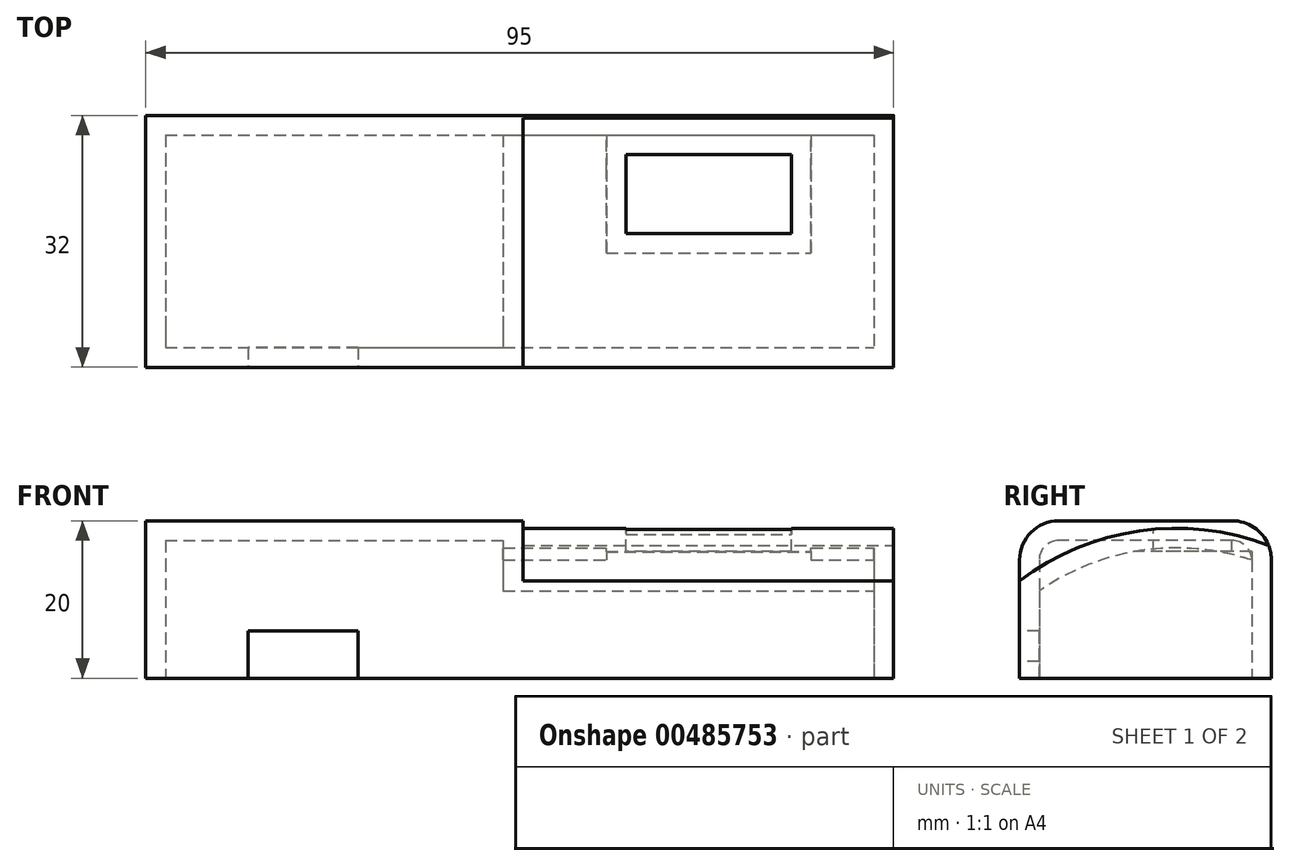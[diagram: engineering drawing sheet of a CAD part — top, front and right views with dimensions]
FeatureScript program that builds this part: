
annotation { "Feature Type Name" : "Feature", "Feature Type Description" : "" }
export const myFeature = defineFeature(function(context is Context, id is Id, definition is map)
    precondition{}
    {
        {
            var Q0;
            Q0=qCreatedBy(makeId("Top.planeOp"),FACE);
            var sketch = newSketch(context, id + "F0", { "sketchPlane" : qUnion([Q0])});
            skLineSegment(sketch, "E0.bottom", {"start": v(19.4, -5.9) * mm, "end": v(114.4, -5.9) * mm});
            skLineSegment(sketch, "E0.top", {"start": v(19.4, -37.9) * mm, "end": v(114.4, -37.9) * mm});
            skLineSegment(sketch, "E0.left", {"start": v(19.4, -5.9) * mm, "end": v(19.4, -37.9) * mm});
            skLineSegment(sketch, "E0.right", {"start": v(114.4, -5.9) * mm, "end": v(114.4, -37.9) * mm});
            skSolve(sketch);
        }
        {
            var Q0;
            Q0=makeQuery(id+"F0.imprint","IMPRINT",FACE,{"disambiguationData":[TD([[makeQuery(id+"F0.imprint","IMPRINT",EDGE,{"derivedFrom":sQuery(id+"F0.wireOp",EDGE,"E0.bottom")}),-1.0]])]});
            extrude(context, id + "F1", {"entities" : qUnion([Q0]), "depth" : 20 * mm});
        }
        {
            var Q0;
            Q0=makeQuery(id+"F1.opExtrude","SWEPT_FACE",FACE,{"disambiguationData":[OSD([sQuery(id+"F0.wireOp",EDGE,"E0.right")])]});
            var sketch = newSketch(context, id + "F2", { "sketchPlane" : qUnion([Q0])});
            skArc(sketch, "E1", {"start": v(-5.9, 16.74) * mm, "mid": v(-22.48, 18.74) * mm, "end": v(-37.9, 12.33) * mm});
            skSolve(sketch);
        }
        {
            var Q0;
            Q0=makeQuery(id+"F1.opExtrude","CAP_EDGE",EDGE,{"disambiguationData":[OSD([sQuery(id+"F0.wireOp",EDGE,"E0.top")])],"isStart":false});
            fillet(context, id + "F3", {"entities" : qUnion([Q0]), "radius" : 5 * mm, "tangentPropagation" : true, "allowEdgeOverflow" : false});
        }
        {
            var Q0;
            Q0=makeQuery(id+"F1.opExtrude","CAP_EDGE",EDGE,{"disambiguationData":[OSD([sQuery(id+"F0.wireOp",EDGE,"E0.bottom")])],"isStart":false});
            fillet(context, id + "F4", {"entities" : qUnion([Q0]), "radius" : 5 * mm, "tangentPropagation" : true, "allowEdgeOverflow" : false});
        }
        {
            var Q0;
            Q0=makeQuery(id+"F1.opExtrude","CAP_FACE",FACE,{"disambiguationData":[OSD([sQuery(id+"F0.wireOp",EDGE,"E0.bottom"),sQuery(id+"F0.wireOp",EDGE,"E0.top"),sQuery(id+"F0.wireOp",EDGE,"E0.left"),sQuery(id+"F0.wireOp",EDGE,"E0.right")])],"isStart":false});
            var sketch = newSketch(context, id + "F5", { "sketchPlane" : qUnion([Q0])});
            skLineSegment(sketch, "E2.bottom", {"start": v(114.4, -10.9) * mm, "end": v(101.4, -10.9) * mm});
            skLineSegment(sketch, "E2.top", {"start": v(114.4, -20.66) * mm, "end": v(101.4, -20.66) * mm});
            skLineSegment(sketch, "E2.left", {"start": v(114.4, -10.9) * mm, "end": v(114.4, -20.66) * mm});
            skLineSegment(sketch, "E2.right", {"start": v(101.4, -10.9) * mm, "end": v(101.4, -20.66) * mm});
            skLineSegment(sketch, "E3.bottom", {"start": v(101.4, -10.9) * mm, "end": v(80.4, -10.9) * mm});
            skLineSegment(sketch, "E3.top", {"start": v(101.4, -20.9) * mm, "end": v(80.4, -20.9) * mm});
            skLineSegment(sketch, "E3.left", {"start": v(101.4, -10.9) * mm, "end": v(101.4, -20.9) * mm});
            skLineSegment(sketch, "E3.right", {"start": v(80.4, -10.9) * mm, "end": v(80.4, -20.9) * mm});
            skSolve(sketch);
        }
        {
            var Q0;
            {var subQ3=sQuery(id+"F5.wireOp",EDGE,"E3.bottom");Q0=makeQuery(id+"F5.imprint","IMPRINT",FACE,{"disambiguationData":[TD([[makeQuery(id+"F5.imprint","IMPRINT",EDGE,{"derivedFrom":subQ3}),1.0]])]});}
            extrude(context, id + "F6", {"entities" : qUnion([Q0]), "operationType" : NewBodyOperationType.REMOVE, "oppositeDirection" : true, "depth" : 25 * mm});
        }
        {
            var Q0;
            {var subQ0=sQuery(id+"F2.wireOp",EDGE,"E1");Q0=makeQuery(id+"F2.imprint","IMPRINT",FACE,{"disambiguationData":[TD([[makeQuery(id+"F2.imprint","IMPRINT",EDGE,{"derivedFrom":subQ0}),-1.0]])]});}
            extrude(context, id + "F7", {"entities" : qUnion([Q0]), "operationType" : NewBodyOperationType.REMOVE, "oppositeDirection" : true, "depth" : 47.1 * mm});
        }
        {
            var Q0;
            Q0=makeQuery(id+"F1.opExtrude","CAP_FACE",FACE,{"disambiguationData":[OSD([sQuery(id+"F0.wireOp",EDGE,"E0.bottom"),sQuery(id+"F0.wireOp",EDGE,"E0.top"),sQuery(id+"F0.wireOp",EDGE,"E0.left"),sQuery(id+"F0.wireOp",EDGE,"E0.right")])],"isStart":true});
            shell(context, id + "F8", {"entities" : qUnion([Q0]), "thickness" : 2.5 * mm});
        }
        {
            var Q0;
            Q0=makeQuery(id+"F1.opExtrude","CAP_FACE",FACE,{"disambiguationData":[OSD([sQuery(id+"F0.wireOp",EDGE,"E0.bottom"),sQuery(id+"F0.wireOp",EDGE,"E0.top"),sQuery(id+"F0.wireOp",EDGE,"E0.left"),sQuery(id+"F0.wireOp",EDGE,"E0.right")])],"isStart":true});
            var sketch = newSketch(context, id + "F9", { "sketchPlane" : qUnion([Q0])});
            skLineSegment(sketch, "E4.bottom", {"start": v(77.9, 8.4) * mm, "end": v(103.9, 8.4) * mm});
            skLineSegment(sketch, "E4.top", {"start": v(77.9, 23.4) * mm, "end": v(103.9, 23.4) * mm});
            skLineSegment(sketch, "E4.left", {"start": v(77.9, 8.4) * mm, "end": v(77.9, 23.4) * mm});
            skLineSegment(sketch, "E4.right", {"start": v(103.9, 8.4) * mm, "end": v(103.9, 23.4) * mm});
            skSolve(sketch);
        }
        {
            var Q0;
            Q0=makeQuery(id+"F9.imprint","IMPRINT",FACE,{"disambiguationData":[TD([[makeQuery(id+"F9.imprint","IMPRINT",EDGE,{"derivedFrom":sQuery(id+"F9.wireOp",EDGE,"E4.bottom")}),1.0]])]});
            extrude(context, id + "F10", {"entities" : qUnion([Q0]), "operationType" : NewBodyOperationType.REMOVE, "oppositeDirection" : true, "depth" : 16.1 * mm});
        }
        {
            var Q0;
            Q0=makeQuery(id+"F1.opExtrude","SWEPT_FACE",FACE,{"disambiguationData":[OSD([sQuery(id+"F0.wireOp",EDGE,"E0.top")])]});
            var sketch = newSketch(context, id + "F11", { "sketchPlane" : qUnion([Q0])});
            skLineSegment(sketch, "E5.bottom", {"start": v(19.4, 10.53) * mm, "end": v(32.4, 10.53) * mm});
            skLineSegment(sketch, "E5.top", {"start": v(19.4, 2.11) * mm, "end": v(32.4, 2.11) * mm});
            skLineSegment(sketch, "E5.left", {"start": v(19.4, 10.53) * mm, "end": v(19.4, 2.11) * mm});
            skLineSegment(sketch, "E5.right", {"start": v(32.4, 10.53) * mm, "end": v(32.4, 2.11) * mm});
            skSolve(sketch);
        }
        {
            var Q0;
            {var subQ3=sQuery(id+"F11.wireOp",EDGE,"E5.bottom");Q0=makeQuery(id+"F11.imprint","IMPRINT",FACE,{"disambiguationData":[TD([[makeQuery(id+"F11.imprint","IMPRINT",EDGE,{"derivedFrom":subQ3}),1.0]])]});}
            var sketch = newSketch(context, id + "F12", { "sketchPlane" : qUnion([Q0])});
            skLineSegment(sketch, "E6.bottom", {"start": v(32.4, 6) * mm, "end": v(46.4, 6) * mm});
            skLineSegment(sketch, "E6.top", {"start": v(32.4, 0) * mm, "end": v(46.4, 0) * mm});
            skLineSegment(sketch, "E6.left", {"start": v(32.4, 6) * mm, "end": v(32.4, 0) * mm});
            skLineSegment(sketch, "E6.right", {"start": v(46.4, 6) * mm, "end": v(46.4, 0) * mm});
            skSolve(sketch);
        }
        {
            var Q0;
            {var subQ7=sQuery(id+"F12.wireOp",EDGE,"E6.top");Q0=makeQuery(id+"F12.imprint","IMPRINT",FACE,{"disambiguationData":[TD([[makeQuery(id+"F12.imprint","IMPRINT",EDGE,{"derivedFrom":subQ7}),1.0]])]});}
            extrude(context, id + "F13", {"entities" : qUnion([Q0]), "operationType" : NewBodyOperationType.REMOVE, "oppositeDirection" : true, "depth" : 25 * mm});
        }
    });
